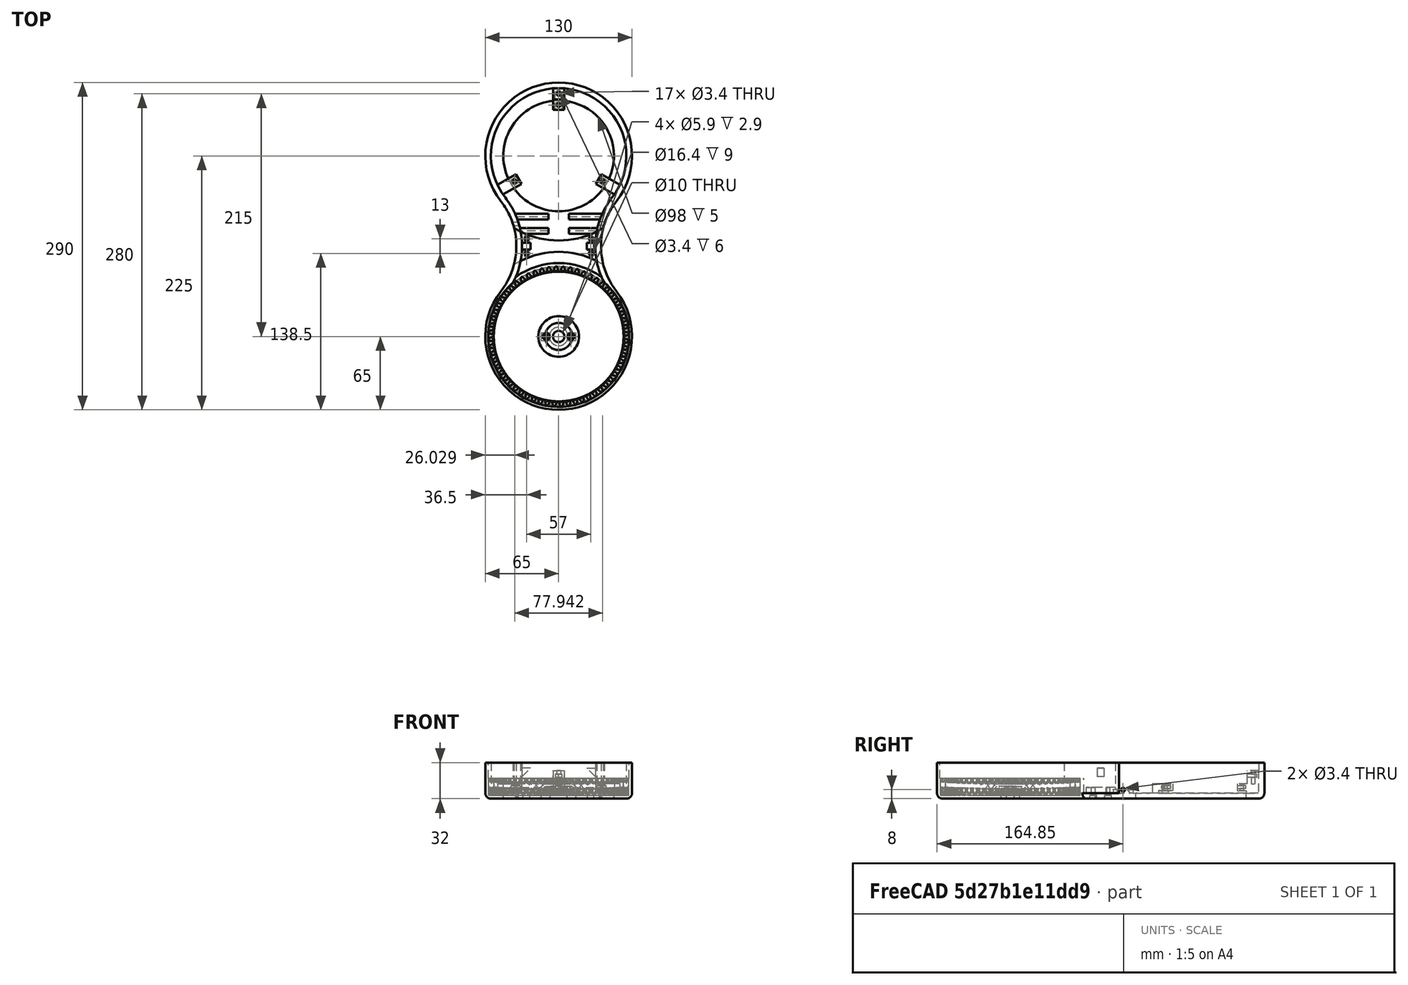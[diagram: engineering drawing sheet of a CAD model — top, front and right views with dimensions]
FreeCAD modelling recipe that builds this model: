
FCSTD DOCUMENT  (FreeCAD 0.16R6703 (Git))
Label: Art2BodyA
License: All rights reserved
LicenseURL: http://en.wikipedia.org/wiki/All_rights_reserved
objects: Part::FeaturePython×27, Part::MultiFuse×11, Sketcher::SketchObject×11, Part::Cut×11, PartDesign::Pad×10, Part::Cylinder×8, Part::Box×4, Part::Prism×1, PartDesign::Revolution×1, Part::Part2DObjectPython×1, Part::Helix×1, Part::Sweep×1, Part::Thickness×1, Part::Fillet×1, App::DocumentObjectGroup×1
note: 100 computed .brp shape members not serialized (recipe doc carries the construction recipe); baked Part::Feature solids carry a one-line shape summary decoded from their .brp

FEATURE [Part::Cylinder] Cylinder  label="M3BoltHead"
  Angle = 360
  Height = 7
  Radius = 2.95
FEATURE [Part::Cylinder] Cylinder001  label="M3BoltBody"
  Angle = 360
  Height = 30
  Placement = pos=(0,0,6) rot=(0,0,1;0rad)
  Radius = 1.7
FEATURE [Part::MultiFuse] Fusion  label="M3Bolt"
  Shapes = -> [Cylinder001,Cylinder]
FEATURE [Sketcher::SketchObject] Sketch003  label="M3NutHousingSketch"
  sketch-geometry (5):
    g0: LineSegment StartX=0 StartY=0 StartZ=0 EndX=1.67432 EndY=2.9 EndZ=0
    g1: LineSegment StartX=1.67432 StartY=2.9 StartZ=0 EndX=21.6743 EndY=2.9 EndZ=0
    g2: LineSegment StartX=21.6743 StartY=2.9 StartZ=0 EndX=21.6743 EndY=-2.9 EndZ=0
    g3: LineSegment StartX=21.6743 StartY=-2.9 StartZ=0 EndX=1.67432 EndY=-2.9 EndZ=0
    g4: LineSegment StartX=1.67432 StartY=-2.9 StartZ=0 EndX=0 EndY=0 EndZ=0
  constraints (14):
    c: Coincident(g-1,g0)
    c: Coincident(g0,g1)
    c: Horizontal(g1)
    c: Coincident(g1,g2)
    c: Vertical(g2)
    c: Coincident(g2,g3)
    c: Horizontal(g3)
    c: Coincident(g3,g4)
    c: Coincident(g4,g0)
    c: Equal(g3,g1)
    c: Equal(g4,g0)
    c: DistanceY(g2) = -5.8
    c: Angle(g-1,g0) = 1.0472
    c: DistanceX(g3) = -20
FEATURE [PartDesign::Pad] Pad002  label="M3NutHousing"
  Length = 2.7
  Length2 = 100
  Sketch = -> Sketch003
  Type = 0
FEATURE [Part::Prism] Prism  label="M3Nut"
  Circumradius = 3.35
  Height = 12
  Polygon = 6
FEATURE [Sketcher::SketchObject] Sketch016
  sketch-geometry (4):
    g0: LineSegment StartX=0 StartY=0 StartZ=0 EndX=0 EndY=18 EndZ=0
    g1: LineSegment StartX=0 StartY=18 StartZ=0 EndX=6 EndY=12 EndZ=0
    g2: LineSegment StartX=6 StartY=12 StartZ=0 EndX=6 EndY=0 EndZ=0
    g3: LineSegment StartX=0 StartY=0 StartZ=0 EndX=6 EndY=0 EndZ=0
  constraints (11):
    c: Coincident(g0,g-1)
    c: Vertical(g0)
    c: Coincident(g1,g0)
    c: Coincident(g2,g1)
    c: PointOnObject(g2,g-1)
    c: Vertical(g2)
    c: Coincident(g3,g-1)
    c: Coincident(g3,g2)
    c: DistanceY(g2) = -12
    c: DistanceX(g3) = 6
    c: Angle(g1,g-1) = 0.785398
FEATURE [PartDesign::Revolution] Revolution003  label="625ZZBearingHousingNoHoles"
  Angle = 360
  Axis = (1,0,0)
  Base = (0,0,0)
  ReferenceAxis = -> Sketch016 [H_Axis]
  Sketch = -> Sketch016
FEATURE [Part::Cylinder] Cylinder1003  label="Bearing625ZZMaster"
  Angle = 360
  Height = 15
  Radius = 8.2
FEATURE [Sketcher::SketchObject] Sketch020
  sketch-geometry (4):
    g0: ArcOfCircle CenterX=0 CenterY=0 CenterZ=0 NormalX=0 NormalY=0 NormalZ=1 Radius=65 StartAngle=2.47872 EndAngle=6.94606
    g1: ArcOfCircle CenterX=102.47 CenterY=80 CenterZ=0 NormalX=0 NormalY=0 NormalZ=1 Radius=65 StartAngle=2.47872 EndAngle=3.80447
    g2: ArcOfCircle CenterX=-102.47 CenterY=80 CenterZ=0 NormalX=0 NormalY=0 NormalZ=1 Radius=65 StartAngle=5.62031 EndAngle=6.94606
    g3: ArcOfCircle CenterX=0 CenterY=160 CenterZ=0 NormalX=0 NormalY=0 NormalZ=1 Radius=65 StartAngle=5.62031 EndAngle=10.0877
  constraints (15):
    c: Coincident(g0,g-1)
    c: Coincident(g1,g0)
    c: Coincident(g2,g0)
    c: Coincident(g3,g1)
    c: Equal(g1,g2)
    c: Equal(g3,g0)
    c: Tangent(g1,g3)
    c: Coincident(g2,g3)
    c: Tangent(g2,g3)
    c: Tangent(g1,g0)
    c: Equal(g0,g2)
    c: Tangent(g0,g2)
    c: DistanceY(g-1,g3) = 160
    c: Radius(g0) = 65
    c: PointOnObject(g3,g-2)
FEATURE [PartDesign::Pad] Pad013
  Length = 32
  Length2 = 100
  Sketch = -> Sketch020
  Type = 0
FEATURE [Part::Part2DObjectPython] InvoluteGear003  # Draft 2D object (typed FeaturePython)
  ExternalGear = true
  HighPrecision = true
  Modules = 2
  NumberOfTeeth = 60
  Placement = pos=(0,0,3) rot=(0,0,1;0rad)
  PressureAngle = 20
FEATURE [Part::Helix] Helix003  label="HelixArt2BodyA"
  Angle = 0
  Height = 15.1
  LocalCoord = 1
  Pitch = 550
  Placement = pos=(0,0,3) rot=(0,0,1;0rad)
  Radius = 1
  Style = 1
FEATURE [Part::Cylinder] Cylinder1009  label="Cylinder016"
  Angle = 360
  Height = 30
  Placement = pos=(0,0,5) rot=(0,0,1;0rad)
  Radius = 62.5
FEATURE [Part::Sweep] Sweep003
  Frenet = true
  Sections = -> [InvoluteGear003]
  Solid = true
  Spine = -> Helix003 [Edge1]
  Transition = 1
FEATURE [Part::Thickness] Thickness001  label="Art2ArmMaster"
  Faces = -> Pad013 [Face6]
  Intersection = false
  Join = 0
  Mode = 0
  SelfIntersection = false
  Value = -5
FEATURE [Part::Cylinder] Cylinder1010  label="Cylinder017"
  Angle = 360
  Height = 13
  Placement = pos=(0,0,5) rot=(0,0,1;0rad)
  Radius = 65
FEATURE [Sketcher::SketchObject] Sketch023
  Placement = pos=(0,0,5) rot=(0,0,1;0rad)
  sketch-geometry (5):
    g0: ArcOfCircle CenterX=0 CenterY=0 CenterZ=0 NormalX=0 NormalY=0 NormalZ=1 Radius=75 StartAngle=1.08528 EndAngle=2.05631
    g1: ArcOfCircle CenterX=0 CenterY=160 CenterZ=0 NormalX=0 NormalY=0 NormalZ=1 Radius=75 StartAngle=4.22687 EndAngle=5.19791
    g2: ArcOfCircle CenterX=115 CenterY=80 CenterZ=0 NormalX=0 NormalY=0 NormalZ=1 Radius=81.1591 StartAngle=2.97238 EndAngle=3.3108
    g3: ArcOfCircle CenterX=-115 CenterY=80 CenterZ=0 NormalX=0 NormalY=0 NormalZ=1 Radius=81.1591 StartAngle=6.11398 EndAngle=6.4524
    g4: LineSegment [constr] StartX=-115 StartY=80 StartZ=0 EndX=115 EndY=80 EndZ=0
  constraints (17):
    c: Coincident(g0,g-1)
    c: PointOnObject(g1,g-2)
    c: Coincident(g2,g1)
    c: Coincident(g2,g0)
    c: Coincident(g3,g1)
    c: Coincident(g3,g0)
    c: Equal(g1,g0)
    c: Equal(g3,g2)
    c: Coincident(g4,g3)
    c: Coincident(g4,g2)
    c: Horizontal(g4)
    c: Radius(g0) = 75
    c: DistanceY(g-1,g1) = 160
    c: DistanceY(g-1,g2) = 80
    c: DistanceX(g4) = 230
    c: DistanceX(g-1,g2) = 115
    c: DistanceX(g0,g0) = 70
FEATURE [PartDesign::Pad] Pad015  label="Art2BodyUnionSupporMaster"
  Length = 5
  Length2 = 100
  Placement = pos=(0,0,5) rot=(0,0,1;0rad)
  Sketch = -> Sketch023
  Type = 0
FEATURE [Part::Cylinder] Cylinder1013  label="Cylinder019"
  Angle = 360
  Height = 10
  Placement = pos=(0,160,0) rot=(0,0,1;0rad)
  Radius = 49
FEATURE [Sketcher::SketchObject] Sketch024
  Placement = pos=(0,0,0) rot=(0.57735,0.57735,0.57735;2.0944rad)
  sketch-geometry (6):
    g0: LineSegment StartX=0 StartY=0 StartZ=0 EndX=0 EndY=8 EndZ=0
    g1: LineSegment StartX=0 StartY=8 StartZ=0 EndX=19 EndY=8 EndZ=0
    g2: LineSegment StartX=19 StartY=8 StartZ=0 EndX=19 EndY=2 EndZ=0
    g3: LineSegment StartX=19 StartY=2 StartZ=0 EndX=11 EndY=2 EndZ=0
    g4: LineSegment StartX=11 StartY=2 StartZ=0 EndX=11 EndY=0 EndZ=0
    g5: LineSegment StartX=11 StartY=0 StartZ=0 EndX=0 EndY=0 EndZ=0
  constraints (17):
    c: Coincident(g-1,g0)
    c: PointOnObject(g0,g-2)
    c: Coincident(g0,g1)
    c: Horizontal(g1)
    c: Coincident(g1,g2)
    c: Vertical(g2)
    c: Coincident(g2,g3)
    c: Horizontal(g3)
    c: Coincident(g3,g4)
    c: Coincident(g4,g5)
    c: Coincident(g5,g0)
    c: Horizontal(g5)
    c: Vertical(g4)
    c: DistanceY(g2) = -6
    c: DistanceX(g3) = -8
    c: DistanceX(g1) = 19
    c: DistanceY(g4) = -2
FEATURE [PartDesign::Pad] Pad016
  Length = 10
  Length2 = 100
  Placement = pos=(0,0,0) rot=(0.57735,0.57735,0.57735;2.0944rad)
  Sketch = -> Sketch024
  Type = 0
FEATURE [Part::FeaturePython] Clone105  label="Clone of M3Bolt030"  # Draft clone (typed FeaturePython)
  Objects = -> [Fusion]
  Placement = pos=(5,15,30) rot=(0,1,0;3.14159rad)
  Scale = (1,1,1)
FEATURE [Part::FeaturePython] Clone106  label="Clone of M3NutHousing008"  # Draft clone (typed FeaturePython)
  Objects = -> [Pad002]
  Placement = pos=(5,11.5,4) rot=(0,0,1;1.5708rad)
  Scale = (1,1,1)
FEATURE [Part::MultiFuse] Fusion045
  Shapes = -> [Clone105,Clone106]
FEATURE [Part::Cut] Cut038
  Base = -> Pad016
  Placement = pos=(5,220,5) rot=(0,0,1;3.14159rad)
  Tool = -> Fusion045
FEATURE [Part::FeaturePython] Array006  # Draft array (typed FeaturePython)
  Angle = 360
  ArrayType = 1
  Axis = (0,0,1)
  Base = -> Cut038
  Center = (0,160,0)
  Fuse = false
  IntervalAxis = (0,0,0)
  IntervalX = (1,0,0)
  IntervalY = (0,1,0)
  IntervalZ = (0,0,0)
  NumberPolar = 3
  NumberX = 2
  NumberY = 2
  NumberZ = 1
FEATURE [Sketcher::SketchObject] Sketch025
  sketch-geometry (3):
    g0: LineSegment StartX=0 StartY=0 StartZ=0 EndX=0 EndY=10 EndZ=0
    g1: LineSegment StartX=0 StartY=10 StartZ=0 EndX=10 EndY=0 EndZ=0
    g2: LineSegment StartX=10 StartY=0 StartZ=0 EndX=0 EndY=0 EndZ=0
  constraints (8):
    c: Coincident(g-1,g0)
    c: PointOnObject(g0,g-2)
    c: Coincident(g0,g1)
    c: PointOnObject(g1,g-1)
    c: Coincident(g1,g2)
    c: Coincident(g2,g0)
    c: DistanceY(g0) = 10
    c: Angle(g1,g2) = 0.785398
FEATURE [PartDesign::Pad] Pad017  label="Art2CoverArmSupportMaster"
  Length = 6
  Length2 = 100
  Sketch = -> Sketch025
  Type = 0
FEATURE [Part::FeaturePython] Clone107  label="Clone of Art2CoverArmSupportMaster"  # Draft clone (typed FeaturePython)
  Objects = -> [Pad017]
  Placement = pos=(-35,77,27) rot=(-1,0,0;1.5708rad)
  Scale = (1,1,1)
FEATURE [Part::FeaturePython] Clone108  label="Clone of Art2CoverArmSupportMaster001"  # Draft clone (typed FeaturePython)
  Objects = -> [Pad017]
  Placement = pos=(35,83,27) rot=(0,-0.707107,0.707107;3.14159rad)
  Scale = (1,1,1)
FEATURE [Part::FeaturePython] Clone109  label="Clone of Art2BodyUnionSupporMaster"  # Draft clone (typed FeaturePython)
  Objects = -> [Pad015]
  Placement = pos=(0,0,5) rot=(0,0,1;0rad)
  Scale = (1,1,1)
FEATURE [Sketcher::SketchObject] Sketch026
  Placement = pos=(0,0,0) rot=(0.57735,0.57735,0.57735;2.0944rad)
  sketch-geometry (8):
    g0: LineSegment StartX=0 StartY=0 StartZ=0 EndX=0 EndY=5 EndZ=0
    g1: LineSegment StartX=0 StartY=5 StartZ=0 EndX=5 EndY=5 EndZ=0
    g2: LineSegment StartX=5 StartY=5 StartZ=0 EndX=2.45 EndY=1.96103 EndZ=0
    g3: LineSegment StartX=2.45 StartY=1.96103 StartZ=0 EndX=15.25 EndY=1.96103 EndZ=0
    g4: LineSegment StartX=15.25 StartY=1.96103 StartZ=0 EndX=12.7 EndY=5 EndZ=0
    g5: LineSegment StartX=12.7 StartY=5 StartZ=0 EndX=17.7 EndY=5 EndZ=0
    g6: LineSegment StartX=17.7 StartY=5 StartZ=0 EndX=17.7 EndY=0 EndZ=0
    g7: LineSegment StartX=17.7 StartY=0 StartZ=0 EndX=0 EndY=0 EndZ=0
  constraints (23):
    c: Coincident(g-1,g0)
    c: PointOnObject(g0,g-2)
    c: Coincident(g0,g1)
    c: Horizontal(g1)
    c: Coincident(g1,g2)
    c: Coincident(g2,g3)
    c: Horizontal(g3)
    c: Coincident(g3,g4)
    c: Coincident(g4,g5)
    c: Horizontal(g5)
    c: Coincident(g5,g6)
    c: PointOnObject(g6,g-1)
    c: Coincident(g6,g7)
    c: Coincident(g7,g0)
    c: Vertical(g6)
    c: Equal(g5,g1)
    c: Equal(g2,g4)
    c: Angle(g3,g2) = 0.872665
    c: DistanceX(g1) = 5
    c: Angle(g4,g3) = 0.872665
    c: DistanceX(g3) = 12.8
    c: DistanceX(g1,g4) = 7.7
    c: DistanceY(g-1,g0) = 5
FEATURE [PartDesign::Pad] Pad018  label="Art2BodyAMilanoMaster"
  Length = 30
  Length2 = 100
  Placement = pos=(0,0,0) rot=(0.57735,0.57735,0.57735;2.0944rad)
  Sketch = -> Sketch026
  Type = 0
FEATURE [Part::Box] Box248  label="Cube012"
  Height = 10
  Length = 10
  Placement = pos=(33.8236,89.3815,3) rot=(0,0,-1;0.261799rad)
  Width = 20
FEATURE [Part::FeaturePython] Clone110  label="Clone of Art2BodyAMilanoMaster"  # Draft clone (typed FeaturePython)
  Objects = -> [Pad018]
  Placement = pos=(-39,91,3) rot=(0.57735,0.57735,0.57735;2.0944rad)
  Scale = (1,1,1)
FEATURE [Part::FeaturePython] Clone111  label="Clone of Art2BodyAMilanoMaster001"  # Draft clone (typed FeaturePython)
  Objects = -> [Pad018]
  Placement = pos=(39,108.7,3) rot=(0.57735,-0.57735,-0.57735;2.0944rad)
  Scale = (1,1,1)
FEATURE [Part::Box] Box249  label="Cube013"
  Height = 10
  Length = 10
  Placement = pos=(-43.4829,86.7933,3) rot=(0,0,1;0.261799rad)
  Width = 20
FEATURE [Part::MultiFuse] Fusion047
  Shapes = -> [Clone110,Clone111]
FEATURE [Part::MultiFuse] Fusion048
  Shapes = -> [Box249,Box248]
FEATURE [Part::FeaturePython] Clone112  label="Clone of M3Bolt031"  # Draft clone (typed FeaturePython)
  Objects = -> [Fusion]
  Placement = pos=(28.5,86.5,-4.1) rot=(0,0,1;3.14159rad)
  Scale = (1,1,1)
FEATURE [Part::FeaturePython] Clone113  label="Clone of M3Bolt032"  # Draft clone (typed FeaturePython)
  Objects = -> [Fusion]
  Placement = pos=(-28.5,86.5,-4.1) rot=(0,0,1;3.14159rad)
  Scale = (1,1,1)
FEATURE [Part::FeaturePython] Clone114  label="Clone of M3Bolt033"  # Draft clone (typed FeaturePython)
  Objects = -> [Fusion]
  Placement = pos=(28.5,73.5,-4.1) rot=(0,0,1;3.14159rad)
  Scale = (1,1,1)
FEATURE [Part::FeaturePython] Clone115  label="Clone of M3Bolt034"  # Draft clone (typed FeaturePython)
  Objects = -> [Fusion]
  Placement = pos=(-28.5,73.5,-4.1) rot=(0,0,1;3.14159rad)
  Scale = (1,1,1)
FEATURE [Part::FeaturePython] Clone116  label="Clone of M3Bolt035"  # Draft clone (typed FeaturePython)
  Objects = -> [Fusion]
  Placement = pos=(-58,99.85,8) rot=(0,1,0;1.5708rad)
  Scale = (1,1,1)
FEATURE [Part::FeaturePython] Clone117  label="Clone of M3Bolt036"  # Draft clone (typed FeaturePython)
  Objects = -> [Fusion]
  Placement = pos=(64,99.85,8) rot=(0,-1,0;1.5708rad)
  Scale = (1,1,1)
FEATURE [Part::MultiFuse] Fusion050
  Shapes = -> [Clone117,Clone112,Clone116,Clone115,Clone113,Clone114]
FEATURE [Part::Box] Box250  label="Cube014"
  Height = 20
  Length = 10
  Width = 10
FEATURE [Part::FeaturePython] Clone118  label="Clone of M3Bolt037"  # Draft clone (typed FeaturePython)
  Objects = -> [Fusion]
  Placement = pos=(5,5,40) rot=(1,0,0;3.14159rad)
  Scale = (1,1,1)
FEATURE [Part::FeaturePython] Clone119  label="Clone of M3NutHousing009"  # Draft clone (typed FeaturePython)
  Objects = -> [Pad002]
  Placement = pos=(1.5,5,14) rot=(0,0,1;0rad)
  Scale = (1,1,1)
FEATURE [Part::MultiFuse] Fusion051
  Shapes = -> [Clone118,Clone119]
FEATURE [Part::Cut] Cut040  label="Art2BodyCoverFix"
  Base = -> Box250
  Tool = -> Fusion051
FEATURE [Part::FeaturePython] Clone136  label="Clone of Bearing625ZZMaster"  # Draft clone (typed FeaturePython)
  Objects = -> [Cylinder1003]
  Placement = pos=(0,0,-6) rot=(0,0,1;0rad)
  Scale = (1,1,1)
FEATURE [Part::Cylinder] Cylinder1015  label="Cylinder021"
  Angle = 360
  Height = 10
  Placement = pos=(0,0,4) rot=(0,0,1;0rad)
  Radius = 5
FEATURE [Part::Box] Box251  label="Cube015"
  Height = 4
  Length = 30.6
  Placement = pos=(-15.3,-3.5,0) rot=(0,0,1;0rad)
  Width = 7
FEATURE [Part::FeaturePython] Clone137  label="Clone of M3Bolt039"  # Draft clone (typed FeaturePython)
  Objects = -> [Fusion]
  Placement = pos=(11,0,-4) rot=(0,0,1;0rad)
  Scale = (1,1,1)
FEATURE [Part::FeaturePython] Clone138  label="Clone of M3Bolt040"  # Draft clone (typed FeaturePython)
  Objects = -> [Fusion]
  Placement = pos=(-11,0,-4) rot=(0,0,1;0rad)
  Scale = (1,1,1)
FEATURE [Part::FeaturePython] Clone139  label="Clone of M3Nut005"  # Draft clone (typed FeaturePython)
  Objects = -> [Prism]
  Placement = pos=(11,0,7) rot=(0,0,1;0.523599rad)
  Scale = (1,1,1)
FEATURE [Part::FeaturePython] Clone140  label="Clone of M3Nut006"  # Draft clone (typed FeaturePython)
  Objects = -> [Prism]
  Placement = pos=(-11,0,7) rot=(0,0,1;0.523599rad)
  Scale = (1,1,1)
FEATURE [Part::MultiFuse] Fusion062  label="Bearing625zzHoles"
  Shapes = -> [Clone140,Clone139,Box251,Clone137,Clone138,Cylinder1015,Clone136]
FEATURE [Part::FeaturePython] Clone146  label="Clone of Art2BodyCoverFix"  # Draft clone (typed FeaturePython)
  Objects = -> [Cut040]
  Placement = pos=(-5,220,5) rot=(0,0,-1;1.5708rad)
  Scale = (1,1,1)
FEATURE [Part::FeaturePython] Clone373  label="Clone of 625ZZBearingHousingNoHoles005"  # Draft clone (typed FeaturePython)
  Objects = -> [Revolution003]
  Placement = pos=(0,0,5) rot=(0,-1,0;1.5708rad)
  Scale = (1,1,1)
FEATURE [Part::FeaturePython] Clone375  label="Clone of Bearing625zzHoles006"  # Draft clone (typed FeaturePython)
  Objects = -> [Fusion062]
  Scale = (1,1,1)
FEATURE [Part::Cylinder] Cylinder1048  label="Cylinder1090"
  Angle = 360
  Height = 2
  Placement = pos=(0,0,3) rot=(0,0,1;0rad)
  Radius = 18
FEATURE [Part::MultiFuse] Fusion141
  Shapes = -> [Cylinder1013,Clone375]
FEATURE [Part::Cut] Cut039
  Base = -> Fusion047
  Tool = -> Fusion048
FEATURE [Part::FeaturePython] Clone441  label="Clone of Art2ArmMaster"  # Draft clone (typed FeaturePython)
  Objects = -> [Thickness001]
  Scale = (1,1,1)
FEATURE [Part::Cut] Cut144  label="Cut177"
  Base = -> Clone441
  Tool = -> Cylinder1009
FEATURE [Part::MultiFuse] Fusion165
  Shapes = -> [Cut144,Cylinder1010]
FEATURE [Part::Cut] Cut145  label="Cut178"
  Base = -> Fusion165
  Tool = -> Sweep003
FEATURE [Part::MultiFuse] Fusion166
  Shapes = -> [Clone373,Cylinder1048,Cut145]
FEATURE [Part::Cut] Cut146  label="Cut179"
  Base = -> Fusion166
  Tool = -> Fusion141
FEATURE [Part::MultiFuse] Fusion167
  Shapes = -> [Cut146,Clone109,Cut039,Array006,Clone146,Clone107,Clone108]
FEATURE [Part::Cut] Cut147  label="Cut180"
  Base = -> Fusion167
  Tool = -> Fusion050
FEATURE [Part::Fillet] Fillet010  label="Art2BodyAMaster"
  Base = -> Cut147
  Edges = 4 edges r=5: [Edge184,Edge185,Edge186,Edge187]
FEATURE [App::DocumentObjectGroup] Group  label="Master"
  Group = -> [Fusion,Pad002,Prism,Revolution003,Cylinder1003,Helix003,Thickness001,Pad015,Pad017,Pad018,Cut040,Fusion062]
FEATURE [Part::FeaturePython] Clone  label="Clone of Art2BodyAMaster"  # Draft clone (typed FeaturePython)
  Objects = -> [Fillet010]
  Scale = (1,1,1)
FEATURE [Part::FeaturePython] Clone442  label="Clone of Art2BodyAMaster001"  # Draft clone (typed FeaturePython)
  Objects = -> [Fillet010]
  Scale = (1,1,1)
FEATURE [Sketcher::SketchObject] Sketch027
  sketch-geometry (4):
    g0: ArcOfCircle CenterX=102.47 CenterY=80 CenterZ=0 NormalX=0 NormalY=0 NormalZ=1 Radius=65 StartAngle=2.47872 EndAngle=3.39457
    g1: ArcOfCircle CenterX=-102.47 CenterY=80 CenterZ=0 NormalX=0 NormalY=0 NormalZ=1 Radius=65 StartAngle=6.03021 EndAngle=6.94606
    g2: ArcOfCircle CenterX=0 CenterY=160 CenterZ=0 NormalX=0 NormalY=0 NormalZ=1 Radius=65.0004 StartAngle=5.62031 EndAngle=10.0877
    g3: ArcOfCircle CenterX=0 CenterY=0 CenterZ=0 NormalX=0 NormalY=0 NormalZ=1 Radius=75 StartAngle=1.01551 EndAngle=2.12608
  constraints (15):
    c: Coincident(g2,g0)
    c: Equal(g0,g1)
    c: Tangent(g0,g2)
    c: Coincident(g1,g2)
    c: Tangent(g1,g2)
    c: DistanceY(g-1,g2) = 160
    c: PointOnObject(g2,g-2)
    c: Coincident(g3,g-1)
    c: Radius(g3) = 75
    c: Symmetric(g0,g1,g-2)
    c: Radius(g0) = 65
    c: DistanceY(g-1,g0) = 80
    c: DistanceX(g-1,g0) = 102.47
    c: Coincident(g0,g3)
    c: Coincident(g3,g1)
FEATURE [PartDesign::Pad] Pad
  Length = 4.75
  Length2 = 100
  Sketch = -> Sketch027
  Type = 0
FEATURE [Sketcher::SketchObject] Sketch029
  Placement = pos=(0,0,-0.25) rot=(0,0,1;0rad)
  sketch-geometry (1):
    g0: Circle CenterX=0 CenterY=160 CenterZ=0 NormalX=0 NormalY=0 NormalZ=1 Radius=75
  constraints (3):
    c: PointOnObject(g0,g-2)
    c: DistanceY(g-1,g0) = 160
    c: Radius(g0) = 75
FEATURE [PartDesign::Pad] Pad019
  Length = 35
  Length2 = 100
  Placement = pos=(0,0,-0.25) rot=(0,0,1;0rad)
  Sketch = -> Sketch029
  Type = 0
FEATURE [Part::Cut] Cut
  Base = -> Clone442
  Tool = -> Pad019
FEATURE [Part::Cut] Cut148  label="Art2BodyASmall1"
  Base = -> Cut
  Tool = -> Pad
FEATURE [Sketcher::SketchObject] Sketch
  Placement = pos=(0,0,-0.25) rot=(0,0,1;0rad)
  sketch-geometry (1):
    g0: Circle CenterX=0 CenterY=0 CenterZ=0 NormalX=0 NormalY=0 NormalZ=1 Radius=75
  constraints (2):
    c: Coincident(g0,g-1)
    c: Radius(g0) = 75
FEATURE [PartDesign::Pad] Pad020
  Length = 35
  Length2 = 100
  Placement = pos=(0,0,-0.25) rot=(0,0,1;0rad)
  Sketch = -> Sketch
  Type = 0
FEATURE [Part::Cut] Cut149
  Base = -> Clone
  Tool = -> Pad020
FEATURE [Sketcher::SketchObject] Sketch030
  Placement = pos=(0,0,4.75) rot=(0,0,1;0rad)
  sketch-geometry (5):
    g0: ArcOfCircle CenterX=0 CenterY=0 CenterZ=0 NormalX=0 NormalY=0 NormalZ=1 Radius=75 StartAngle=0.927295 EndAngle=2.2143
    g1: ArcOfCircle CenterX=0 CenterY=160 CenterZ=0 NormalX=0 NormalY=0 NormalZ=1 Radius=75 StartAngle=4.06889 EndAngle=5.35589
    g2: ArcOfCircle CenterX=115 CenterY=80 CenterZ=0 NormalX=0 NormalY=0 NormalZ=1 Radius=72.8011 StartAngle=2.86329 EndAngle=3.41989
    g3: ArcOfCircle CenterX=-115 CenterY=80 CenterZ=0 NormalX=0 NormalY=0 NormalZ=1 Radius=72.8011 StartAngle=6.00489 EndAngle=6.56148
    g4: LineSegment [constr] StartX=-115 StartY=80 StartZ=0 EndX=115 EndY=80 EndZ=0
  constraints (17):
    c: Coincident(g0,g-1)
    c: PointOnObject(g1,g-2)
    c: Coincident(g2,g1)
    c: Coincident(g2,g0)
    c: Coincident(g3,g1)
    c: Coincident(g3,g0)
    c: Equal(g1,g0)
    c: Equal(g3,g2)
    c: Coincident(g4,g3)
    c: Coincident(g4,g2)
    c: Horizontal(g4)
    c: Radius(g0) = 75
    c: DistanceY(g-1,g1) = 160
    c: DistanceY(g-1,g2) = 80
    c: DistanceX(g4) = 230
    c: DistanceX(g-1,g2) = 115
    c: DistanceX(g0,g0) = 90
FEATURE [PartDesign::Pad] Pad021
  Length = 35
  Length2 = 100
  Placement = pos=(0,0,4.75) rot=(0,0,1;0rad)
  Sketch = -> Sketch030
  Type = 0
FEATURE [Part::Cut] Cut150  label="Art2BodyASmall2"
  Base = -> Cut149
  Tool = -> Pad021
